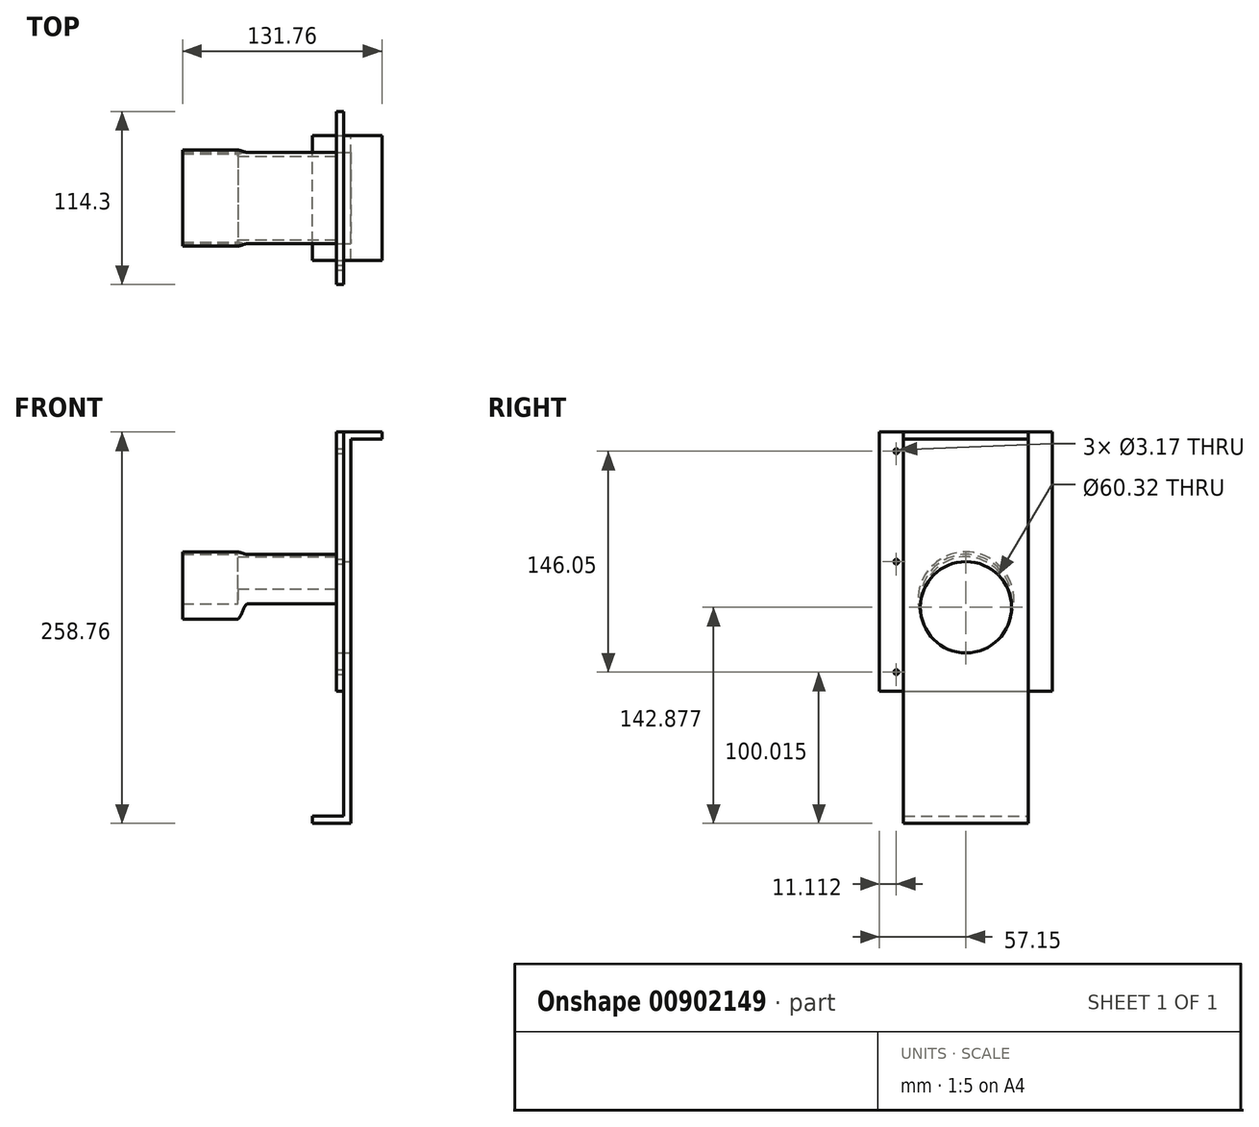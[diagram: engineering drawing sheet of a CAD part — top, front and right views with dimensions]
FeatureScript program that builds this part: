
annotation { "Feature Type Name" : "Feature", "Feature Type Description" : "" }
export const myFeature = defineFeature(function(context is Context, id is Id, definition is map)
    precondition{}
    {
        {
            var Q0;
            Q0=qCreatedBy(makeId("Top.planeOp"),FACE);
            var sketch = newSketch(context, id + "F0", { "sketchPlane" : qUnion([Q0])});
            skLineSegment(sketch, "E0", {"start": v(0, 28.58) * mm, "end": v(0, 30.16) * mm});
            skLineSegment(sketch, "E1", {"start": v(0, 30.16) * mm, "end": v(-63.5, 30.16) * mm});
            skLineSegment(sketch, "E2", {"start": v(-63.5, 30.16) * mm, "end": v(-63.5, 31.75) * mm});
            skLineSegment(sketch, "E3", {"start": v(-63.5, 31.75) * mm, "end": v(-101.6, 31.75) * mm});
            skLineSegment(sketch, "E4", {"start": v(-101.6, 31.75) * mm, "end": v(-101.6, 30.16) * mm});
            skLineSegment(sketch, "E5", {"start": v(-101.6, 30.16) * mm, "end": v(-65.09, 30.16) * mm});
            skLineSegment(sketch, "E6", {"start": v(-65.09, 30.16) * mm, "end": v(-65.09, 28.58) * mm});
            skLineSegment(sketch, "E7", {"start": v(-65.09, 28.58) * mm, "end": v(0, 28.58) * mm});
            skLineSegment(sketch, "E8", {"start": v(0, 0) * mm, "end": v(0, 28.58) * mm, "construction": true});
            skSolve(sketch);
        }
        {
            var Q0;
            Q0=qCreatedBy(makeId("Front.planeOp"),FACE);
            var sketch = newSketch(context, id + "F1", { "sketchPlane" : qUnion([Q0])});
            skLineSegment(sketch, "E9", {"start": v(0, 0) * mm, "end": v(-62.19, 0) * mm, "construction": true});
            skSolve(sketch);
        }
        {
            var Q0;
            Q0=makeQuery(id+"F0.imprint","IMPRINT",FACE,{"disambiguationData":[TD([[makeQuery(id+"F0.imprint","IMPRINT",EDGE,{"derivedFrom":sQuery(id+"F0.wireOp",EDGE,"E0")}),1.0]])]});
            var Q1;
            Q1=sQuery(id+"F1.wireOp",EDGE,"E9");
            revolve(context, id + "F2", {"surfaceOperationType" : NewSurfaceOperationType.NEW, "entities" : qUnion([Q0]), "axis" : qUnion([Q1]), "revolveType" : RevolveType.FULL});
        }
        {
            var Q0;
            Q0=makeQuery(id+"F2.opRevolve","SWEPT_EDGE",EDGE,{"disambiguationData":[OSD([sQuery(id+"F0.wireOp",EDGE,"E1"),sQuery(id+"F0.wireOp",EDGE,"E2")])]});
            fillet(context, id + "F3", {"entities" : qUnion([Q0]), "radius" : 10.16 * mm, "tangentPropagation" : true, "allowEdgeOverflow" : false});
        }
        {
            var Q0;
            Q0=makeQuery(id+"F3.opFillet","BLEND_EDGE",EDGE,{"blendedFrom":[makeQuery(id+"F2.opRevolve","SWEPT_EDGE",EDGE,{"disambiguationData":[OSD([sQuery(id+"F0.wireOp",EDGE,"E1"),sQuery(id+"F0.wireOp",EDGE,"E2")])]}),makeQuery(id+"F2.opRevolve","SWEPT_FACE",FACE,{"disambiguationData":[OSD([sQuery(id+"F0.wireOp",EDGE,"E3")])]})],"blendedInto":[makeQuery(id+"F2.opRevolve","SWEPT_FACE",FACE,{"disambiguationData":[OSD([sQuery(id+"F0.wireOp",EDGE,"E3")])]})]});
            fillet(context, id + "F4", {"entities" : qUnion([Q0]), "radius" : 10.16 * mm, "tangentPropagation" : true, "allowEdgeOverflow" : false});
        }
        {
            var Q0;
            Q0=qCreatedBy(makeId("Right.planeOp"),FACE);
            var sketch = newSketch(context, id + "F5", { "sketchPlane" : qUnion([Q0])});
            skLineSegment(sketch, "E10", {"start": v(0, 0) * mm, "end": v(0, -60.32) * mm, "construction": true});
            skPoint(sketch, "E11.endSnap0", {"position": v(26.59, -60.32) * mm});
            skPoint(sketch, "E11.end.orphan", {"position": v(26.59, -78.64) * mm});
            skPoint(sketch, "E11.start.orphan", {"position": v(53.17, -60.32) * mm});
            skLineSegment(sketch, "E12", {"start": v(0, -60.32) * mm, "end": v(-57.15, -60.32) * mm, "construction": true});
            skLineSegment(sketch, "E13.bottom", {"start": v(-57.15, -60.32) * mm, "end": v(57.15, -60.32) * mm});
            skLineSegment(sketch, "E13.top", {"start": v(-57.15, 111.12) * mm, "end": v(57.15, 111.12) * mm});
            skLineSegment(sketch, "E13.left", {"start": v(-57.15, -60.32) * mm, "end": v(-57.15, 111.13) * mm});
            skLineSegment(sketch, "E13.right", {"start": v(57.15, -60.33) * mm, "end": v(57.15, 111.12) * mm});
            skSolve(sketch);
        }
        {
            var Q0;
            Q0=makeQuery(id+"F5.imprint","IMPRINT",FACE,{"disambiguationData":[TD([[makeQuery(id+"F5.imprint","IMPRINT",EDGE,{"derivedFrom":sQuery(id+"F5.wireOp",EDGE,"E13.bottom")}),1.0]])]});
            extrude(context, id + "F6", {"entities" : qUnion([Q0]), "operationType" : NewBodyOperationType.ADD, "depth" : 4.76 * mm, "offsetDistance" : 25.4 * mm});
        }
        {
            var Q0;
            Q0=makeQuery(id+"F6.boolean.opBoolean","SPLIT",FACE,{"disambiguationData":[TD([makeQuery(id+"F2.opRevolve","SWEPT_FACE",FACE,{"disambiguationData":[OSD([sQuery(id+"F0.wireOp",EDGE,"E7")])]})])],"derivedFrom":makeQuery(id+"F6.opExtrude","CAP_FACE",FACE,{"disambiguationData":[OSD([sQuery(id+"F5.wireOp",EDGE,"E13.bottom"),sQuery(id+"F5.wireOp",EDGE,"E13.top"),sQuery(id+"F5.wireOp",EDGE,"E13.left"),sQuery(id+"F5.wireOp",EDGE,"E13.right")])],"isStart":true})});
            extrude(context, id + "F7", {"entities" : qUnion([Q0]), "operationType" : NewBodyOperationType.REMOVE, "endBound" : BoundingType.THROUGH_ALL, "oppositeDirection" : true, "depth" : 25.4 * mm, "offsetDistance" : 25.4 * mm});
        }
        {
            var Q0;
            Q0=makeQuery(id+"F6.opExtrude","CAP_FACE",FACE,{"disambiguationData":[OSD([sQuery(id+"F5.wireOp",EDGE,"E13.bottom"),sQuery(id+"F5.wireOp",EDGE,"E13.top"),sQuery(id+"F5.wireOp",EDGE,"E13.left"),sQuery(id+"F5.wireOp",EDGE,"E13.right")])],"isStart":false});
            var sketch = newSketch(context, id + "F8", { "sketchPlane" : qUnion([Q0])});
            skLineSegment(sketch, "E14", {"start": v(-57.15, -60.32) * mm, "end": v(-46.04, -60.32) * mm, "construction": true});
            skLineSegment(sketch, "E15", {"start": v(-46.04, -60.32) * mm, "end": v(-46.04, -47.62) * mm, "construction": true});
            skCircle(sketch, "E16", {"center": v(-46.04, -47.62) * mm, "radius": 1.59 * mm});
            skLineSegment(sketch, "E17", {"start": v(-46.04, -47.62) * mm, "end": v(-46.04, 25.4) * mm, "construction": true});
            skLineSegment(sketch, "E18", {"start": v(-46.04, 25.4) * mm, "end": v(-46.04, 98.43) * mm, "construction": true});
            skCircle(sketch, "E19", {"center": v(-46.04, 25.4) * mm, "radius": 1.59 * mm});
            skCircle(sketch, "E20", {"center": v(-46.04, 98.43) * mm, "radius": 1.59 * mm});
            skSolve(sketch);
        }
        {
            var Q0;
            Q0 = qSketchRegion(id + "F8", true);
            extrude(context, id + "F9", {"entities" : qUnion([Q0]), "operationType" : NewBodyOperationType.REMOVE, "endBound" : BoundingType.THROUGH_ALL, "oppositeDirection" : true, "depth" : 25.4 * mm, "offsetDistance" : 25.4 * mm});
        }
        {
            var Q0;
            Q0=qCreatedBy(makeId("Front.planeOp"),FACE);
            var sketch = newSketch(context, id + "F10", { "sketchPlane" : qUnion([Q0])});
            skLineSegment(sketch, "E21", {"start": v(4.76, -142.88) * mm, "end": v(4.76, 111.13) * mm});
            skLineSegment(sketch, "E22", {"start": v(4.76, 111.12) * mm, "end": v(30.16, 111.12) * mm});
            skLineSegment(sketch, "E23", {"start": v(30.16, 111.12) * mm, "end": v(30.16, 106.36) * mm});
            skLineSegment(sketch, "E24", {"start": v(30.16, 106.36) * mm, "end": v(9.53, 106.36) * mm});
            skLineSegment(sketch, "E25", {"start": v(9.53, 106.36) * mm, "end": v(9.53, -147.64) * mm});
            skLineSegment(sketch, "E26", {"start": v(9.53, -147.64) * mm, "end": v(-15.87, -147.64) * mm});
            skLineSegment(sketch, "E27", {"start": v(-15.87, -147.64) * mm, "end": v(-15.87, -142.88) * mm});
            skLineSegment(sketch, "E28", {"start": v(-15.87, -142.88) * mm, "end": v(4.76, -142.88) * mm});
            skLineSegment(sketch, "E29", {"start": v(4.76, -142.88) * mm, "end": v(4.76, -142.88) * mm});
            skSolve(sketch);
        }
        {
            var Q0;
            Q0 = qSketchRegion(id + "F10", true);
            extrude(context, id + "F11", {"entities" : qUnion([Q0]), "depth" : 82.55 * mm, "offsetDistance" : 25.4 * mm, "symmetric" : true});
        }
        {
            var Q0;
            Q0=makeQuery(id+"F11.opExtrude","SWEPT_FACE",FACE,{"disambiguationData":[OSD([sQuery(id+"F10.wireOp",EDGE,"E25")])]});
            var sketch = newSketch(context, id + "F12", { "sketchPlane" : qUnion([Q0])});
            skLineSegment(sketch, "E30", {"start": v(0, 106.36) * mm, "end": v(0, -4.76) * mm, "construction": true});
            skCircle(sketch, "E31", {"center": v(0, -4.76) * mm, "radius": 30.16 * mm});
            skSolve(sketch);
        }
        {
            var Q0;
            Q0=makeQuery(id+"F12.imprint","IMPRINT",FACE,{"disambiguationData":[TD([[makeQuery(id+"F12.imprint","IMPRINT",EDGE,{"derivedFrom":sQuery(id+"F12.wireOp",EDGE,"E31")}),1.0]])]});
            extrude(context, id + "F13", {"entities" : qUnion([Q0]), "operationType" : NewBodyOperationType.REMOVE, "endBound" : BoundingType.THROUGH_ALL, "oppositeDirection" : true, "depth" : 25.4 * mm, "offsetDistance" : 25.4 * mm});
        }
    });
